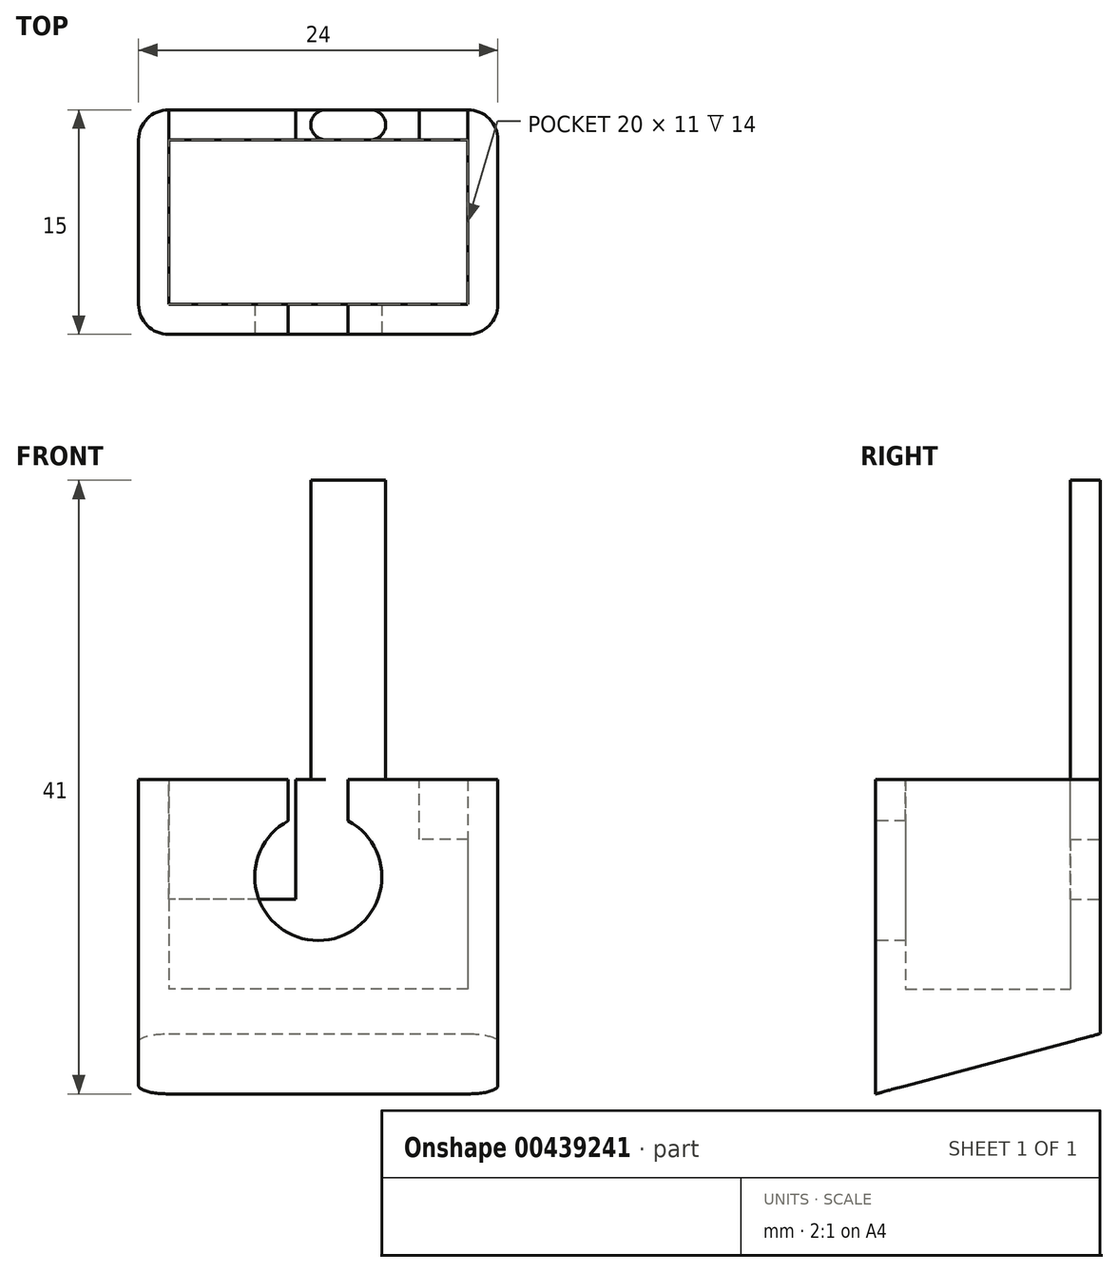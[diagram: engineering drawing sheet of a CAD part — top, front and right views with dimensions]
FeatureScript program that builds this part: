
annotation { "Feature Type Name" : "Feature", "Feature Type Description" : "" }
export const myFeature = defineFeature(function(context is Context, id is Id, definition is map)
    precondition{}
    {
        {
            var Q0;
            Q0=qCreatedBy(makeId("Top.planeOp"),FACE);
            var sketch = newSketch(context, id + "F0", { "sketchPlane" : qUnion([Q0])});
            skLineSegment(sketch, "E0.bottom", {"start": v(12, -7.5) * mm, "end": v(-12, -7.5) * mm});
            skLineSegment(sketch, "E0.top", {"start": v(12, 7.5) * mm, "end": v(-12, 7.5) * mm});
            skLineSegment(sketch, "E0.left", {"start": v(12, -7.5) * mm, "end": v(12, 7.5) * mm});
            skLineSegment(sketch, "E0.right", {"start": v(-12, -7.5) * mm, "end": v(-12, 7.5) * mm});
            skPoint(sketch, "E0.middle", {"position": v(0, 0) * mm});
            skSolve(sketch);
        }
        {
            var Q0;
            Q0=qSketchRegion(id+"F0",true);
            extrude(context, id + "F1", {"entities" : qUnion([Q0]), "flatOperationType" : FlatOperationType.REMOVE, "depth" : 16 * mm, "offsetDistance" : 25 * mm, "domain" : OperationDomain.MODEL});
        }
        {
            var Q0;
            Q0=makeQuery(id+"F1.opExtrude","CAP_FACE",FACE,{"disambiguationData":[OSD([sQuery(id+"F0.wireOp",EDGE,"E0.bottom"),sQuery(id+"F0.wireOp",EDGE,"E0.top"),sQuery(id+"F0.wireOp",EDGE,"E0.left"),sQuery(id+"F0.wireOp",EDGE,"E0.right")])],"isStart":false});
            shell(context, id + "F2", {"entities" : qUnion([Q0]), "thickness" : 2 * mm});
        }
        {
            var Q0;
            Q0=makeQuery(id+"F1.opExtrude","SWEPT_FACE",FACE,{"disambiguationData":[OSD([sQuery(id+"F0.wireOp",EDGE,"E0.bottom")])]});
            var sketch = newSketch(context, id + "F3", { "sketchPlane" : qUnion([Q0])});
            skArc(sketch, "E1", {"start": v(-2, 13.25) * mm, "mid": v(0, 5.25) * mm, "end": v(2, 13.25) * mm});
            skLineSegment(sketch, "E2", {"start": v(-2, 13.25) * mm, "end": v(-2, 16) * mm});
            skLineSegment(sketch, "E3.MirrorCS", {"start": v(2, 13.25) * mm, "end": v(2, 16) * mm});
            skSolve(sketch);
        }
        {
            var Q0;
            Q0=makeQuery(id+"F3.imprint","IMPRINT",FACE,{"disambiguationData":[TD([[makeQuery(id+"F3.imprint","IMPRINT",EDGE,{"derivedFrom":sQuery(id+"F3.wireOp",EDGE,"E1")}),1.0]])]});
            extrude(context, id + "F4", {"entities" : qUnion([Q0]), "operationType" : NewBodyOperationType.REMOVE, "oppositeDirection" : true, "depth" : 5 * mm, "offsetDistance" : 25 * mm});
        }
        {
            var Q0;
            Q0=makeQuery(id+"F1.opExtrude","CAP_FACE",FACE,{"disambiguationData":[OSD([sQuery(id+"F0.wireOp",EDGE,"E0.bottom"),sQuery(id+"F0.wireOp",EDGE,"E0.top"),sQuery(id+"F0.wireOp",EDGE,"E0.left"),sQuery(id+"F0.wireOp",EDGE,"E0.right")])],"isStart":false});
            var sketch = newSketch(context, id + "F5", { "sketchPlane" : qUnion([Q0])});
            skLineSegment(sketch, "E4.bottom", {"start": v(-0.5, 7.5) * mm, "end": v(4.5, 7.5) * mm});
            skLineSegment(sketch, "E4.top", {"start": v(-0.5, 5.5) * mm, "end": v(4.5, 5.5) * mm});
            skLineSegment(sketch, "E4.left", {"start": v(-0.5, 7.5) * mm, "end": v(-0.5, 5.5) * mm});
            skLineSegment(sketch, "E4.right", {"start": v(4.5, 7.5) * mm, "end": v(4.5, 5.5) * mm});
            skSolve(sketch);
        }
        {
            var Q0;
            Q0=makeQuery(id+"F5.imprint","IMPRINT",FACE,{"disambiguationData":[TD([[makeQuery(id+"F5.imprint","IMPRINT",EDGE,{"derivedFrom":sQuery(id+"F5.wireOp",EDGE,"E4.bottom")}),1.0]])]});
            extrude(context, id + "F6", {"entities" : qUnion([Q0]), "operationType" : NewBodyOperationType.ADD, "depth" : 20 * mm});
        }
        {
            var Q0;
            Q0=makeQuery(id+"F1.opExtrude","CAP_FACE",FACE,{"disambiguationData":[OSD([sQuery(id+"F0.wireOp",EDGE,"E0.bottom"),sQuery(id+"F0.wireOp",EDGE,"E0.top"),sQuery(id+"F0.wireOp",EDGE,"E0.left"),sQuery(id+"F0.wireOp",EDGE,"E0.right")])],"isStart":true});
            extrude(context, id + "F7", {"entities" : qUnion([Q0]), "operationType" : NewBodyOperationType.ADD, "depth" : 5 * mm, "offsetDistance" : 25 * mm});
        }
        {
            var Q0;
            {var subQ0=sQuery(id+"F0.wireOp",EDGE,"E0.left");Q0=makeQuery(id+"F7.boolean.opBoolean","MERGE",FACE,{"derivedFrom":[makeQuery(id+"F1.opExtrude","SWEPT_FACE",FACE,{"disambiguationData":[OSD([subQ0])]}),makeQuery(id+"F7.opExtrude","SWEPT_FACE",FACE,{"disambiguationData":[OSD([subQ0])]})]});}
            var sketch = newSketch(context, id + "F8", { "sketchPlane" : qUnion([Q0])});
            skLineSegment(sketch, "E5", {"start": v(-7.5, -5) * mm, "end": v(7.5, -0.98) * mm});
            skSolve(sketch);
        }
        {
            var Q0;
            Q0=makeQuery(id+"F6.opExtrude","SWEPT_EDGE",EDGE,{"disambiguationData":[OSD([sQuery(id+"F0.wireOp",EDGE,"E0.top"),sQuery(id+"F5.wireOp",EDGE,"E4.top"),sQuery(id+"F5.wireOp",EDGE,"E4.right")])]});
            var Q1;
            Q1=makeQuery(id+"F6.opExtrude","SWEPT_EDGE",EDGE,{"disambiguationData":[OSD([sQuery(id+"F0.wireOp",EDGE,"E0.top"),sQuery(id+"F5.wireOp",EDGE,"E4.bottom"),sQuery(id+"F5.wireOp",EDGE,"E4.right")])]});
            var Q2;
            Q2=makeQuery(id+"F6.opExtrude","SWEPT_EDGE",EDGE,{"disambiguationData":[OSD([sQuery(id+"F0.wireOp",EDGE,"E0.top"),sQuery(id+"F5.wireOp",EDGE,"E4.top"),sQuery(id+"F5.wireOp",EDGE,"E4.left")])]});
            var Q3;
            Q3=makeQuery(id+"F6.opExtrude","SWEPT_EDGE",EDGE,{"disambiguationData":[OSD([sQuery(id+"F0.wireOp",EDGE,"E0.top"),sQuery(id+"F5.wireOp",EDGE,"E4.bottom"),sQuery(id+"F5.wireOp",EDGE,"E4.left")])]});
            fillet(context, id + "F9", {"entities" : qUnion([Q0, Q1, Q2, Q3]), "radius" : 1 * mm, "tangentPropagation" : true, "allowEdgeOverflow" : false});
        }
        {
            var Q0;
            Q0=makeQuery(id+"F1.opExtrude","SWEPT_EDGE",EDGE,{"disambiguationData":[OSD([sQuery(id+"F0.wireOp",EDGE,"E0.bottom"),sQuery(id+"F0.wireOp",EDGE,"E0.left")])]});
            var Q1;
            Q1=makeQuery(id+"F1.opExtrude","SWEPT_EDGE",EDGE,{"disambiguationData":[OSD([sQuery(id+"F0.wireOp",EDGE,"E0.bottom"),sQuery(id+"F0.wireOp",EDGE,"E0.right")])]});
            var Q2;
            Q2=makeQuery(id+"F1.opExtrude","SWEPT_EDGE",EDGE,{"disambiguationData":[OSD([sQuery(id+"F0.wireOp",EDGE,"E0.top"),sQuery(id+"F0.wireOp",EDGE,"E0.right")])]});
            var Q3;
            {var subQ0=sQuery(id+"F0.wireOp",EDGE,"E0.left");var subQ1=sQuery(id+"F0.wireOp",EDGE,"E0.top");Q3=makeQuery(id+"FvEb3cs1EhIj02q_1.boolean.opBoolean","SPLIT",EDGE,{"disambiguationData":[TD([makeQuery(id+"F1.opExtrude","CAP_FACE",FACE,{"disambiguationData":[OSD([sQuery(id+"F0.wireOp",EDGE,"E0.bottom"),subQ1,subQ0,sQuery(id+"F0.wireOp",EDGE,"E0.right")])],"isStart":false})])],"derivedFrom":makeQuery(id+"F1.opExtrude","SWEPT_EDGE",EDGE,{"disambiguationData":[OSD([subQ1,subQ0])]})});}
            var Q4;
            {var subQ0=sQuery(id+"F0.wireOp",EDGE,"E0.left");var subQ1=sQuery(id+"F0.wireOp",EDGE,"E0.top");Q4=makeQuery(id+"FvEb3cs1EhIj02q_1.boolean.opBoolean","SPLIT",EDGE,{"disambiguationData":[TD([makeQuery(id+"F1.opExtrude","CAP_FACE",FACE,{"disambiguationData":[OSD([sQuery(id+"F0.wireOp",EDGE,"E0.bottom"),subQ1,subQ0,sQuery(id+"F0.wireOp",EDGE,"E0.right")])],"isStart":true})])],"derivedFrom":makeQuery(id+"F1.opExtrude","SWEPT_EDGE",EDGE,{"disambiguationData":[OSD([subQ1,subQ0])]})});}
            fillet(context, id + "F10", {"entities" : qUnion([Q0, Q1, Q2, Q3, Q4]), "radius" : 2 * mm, "tangentPropagation" : true, "allowEdgeOverflow" : false});
        }
        {
            var Q0;
            {var subQ0=sQuery(id+"F0.wireOp",EDGE,"E0.bottom");var subQ1=sQuery(id+"F0.wireOp",EDGE,"E0.top");var subQ2=sQuery(id+"F0.wireOp",EDGE,"E0.right");Q0=makeQuery(id+"F6.boolean.opBoolean","SPLIT",FACE,{"disambiguationData":[TD([makeQuery(id+"F1.opExtrude","SWEPT_FACE",FACE,{"disambiguationData":[OSD([subQ2])]})])],"derivedFrom":makeQuery(id+"F1.opExtrude","CAP_FACE",FACE,{"disambiguationData":[OSD([subQ0,subQ1,sQuery(id+"F0.wireOp",EDGE,"E0.left"),subQ2])],"isStart":false})});}
            var sketch = newSketch(context, id + "F11", { "sketchPlane" : qUnion([Q0])});
            skLineSegment(sketch, "E6", {"start": v(-10, 5.5) * mm, "end": v(-10, 7.5) * mm});
            skLineSegment(sketch, "E7", {"start": v(-1.5, 7.5) * mm, "end": v(-1.5, 5.5) * mm});
            skSolve(sketch);
        }
        {
            var Q0;
            {var subQ0=sQuery(id+"F11.wireOp",EDGE,"E6");Q0=makeQuery(id+"F11.imprint","IMPRINT",FACE,{"disambiguationData":[TD([[makeQuery(id+"F11.imprint","IMPRINT",EDGE,{"derivedFrom":subQ0}),-1.0]])]});}
            extrude(context, id + "F12", {"entities" : qUnion([Q0]), "operationType" : NewBodyOperationType.REMOVE, "oppositeDirection" : true, "depth" : 8 * mm, "offsetDistance" : 25 * mm});
        }
        {
            var Q0;
            {var subQ0=sQuery(id+"F0.wireOp",EDGE,"E0.bottom");var subQ1=sQuery(id+"F0.wireOp",EDGE,"E0.left");var subQ2=sQuery(id+"F0.wireOp",EDGE,"E0.top");Q0=makeQuery(id+"F6.boolean.opBoolean","SPLIT",FACE,{"disambiguationData":[TD([makeQuery(id+"F1.opExtrude","SWEPT_FACE",FACE,{"disambiguationData":[OSD([subQ1])]})])],"derivedFrom":makeQuery(id+"F1.opExtrude","CAP_FACE",FACE,{"disambiguationData":[OSD([subQ0,subQ2,subQ1,sQuery(id+"F0.wireOp",EDGE,"E0.right")])],"isStart":false})});}
            var sketch = newSketch(context, id + "F13", { "sketchPlane" : qUnion([Q0])});
            skLineSegment(sketch, "E8", {"start": v(10, 5.5) * mm, "end": v(10, 7.5) * mm});
            skLineSegment(sketch, "E9", {"start": v(6.75, 5.5) * mm, "end": v(6.75, 7.5) * mm});
            skSolve(sketch);
        }
        {
            var Q0;
            {var subQ0=sQuery(id+"F13.wireOp",EDGE,"E8");Q0=makeQuery(id+"F13.imprint","IMPRINT",FACE,{"disambiguationData":[TD([[makeQuery(id+"F13.imprint","IMPRINT",EDGE,{"derivedFrom":subQ0}),1.0]])]});}
            extrude(context, id + "F14", {"entities" : qUnion([Q0]), "operationType" : NewBodyOperationType.REMOVE, "oppositeDirection" : true, "depth" : 4 * mm, "offsetDistance" : 25 * mm});
        }
        {
            var Q0;
            {var subQ0=sQuery(id+"F8.wireOp",EDGE,"E5");Q0=makeQuery(id+"F8.imprint","IMPRINT",FACE,{"disambiguationData":[TD([[makeQuery(id+"F8.imprint","IMPRINT",EDGE,{"derivedFrom":subQ0}),-1.0]])]});}
            extrude(context, id + "F15", {"entities" : qUnion([Q0]), "operationType" : NewBodyOperationType.REMOVE, "oppositeDirection" : true, "depth" : 25 * mm, "offsetDistance" : 25 * mm});
        }
    });
